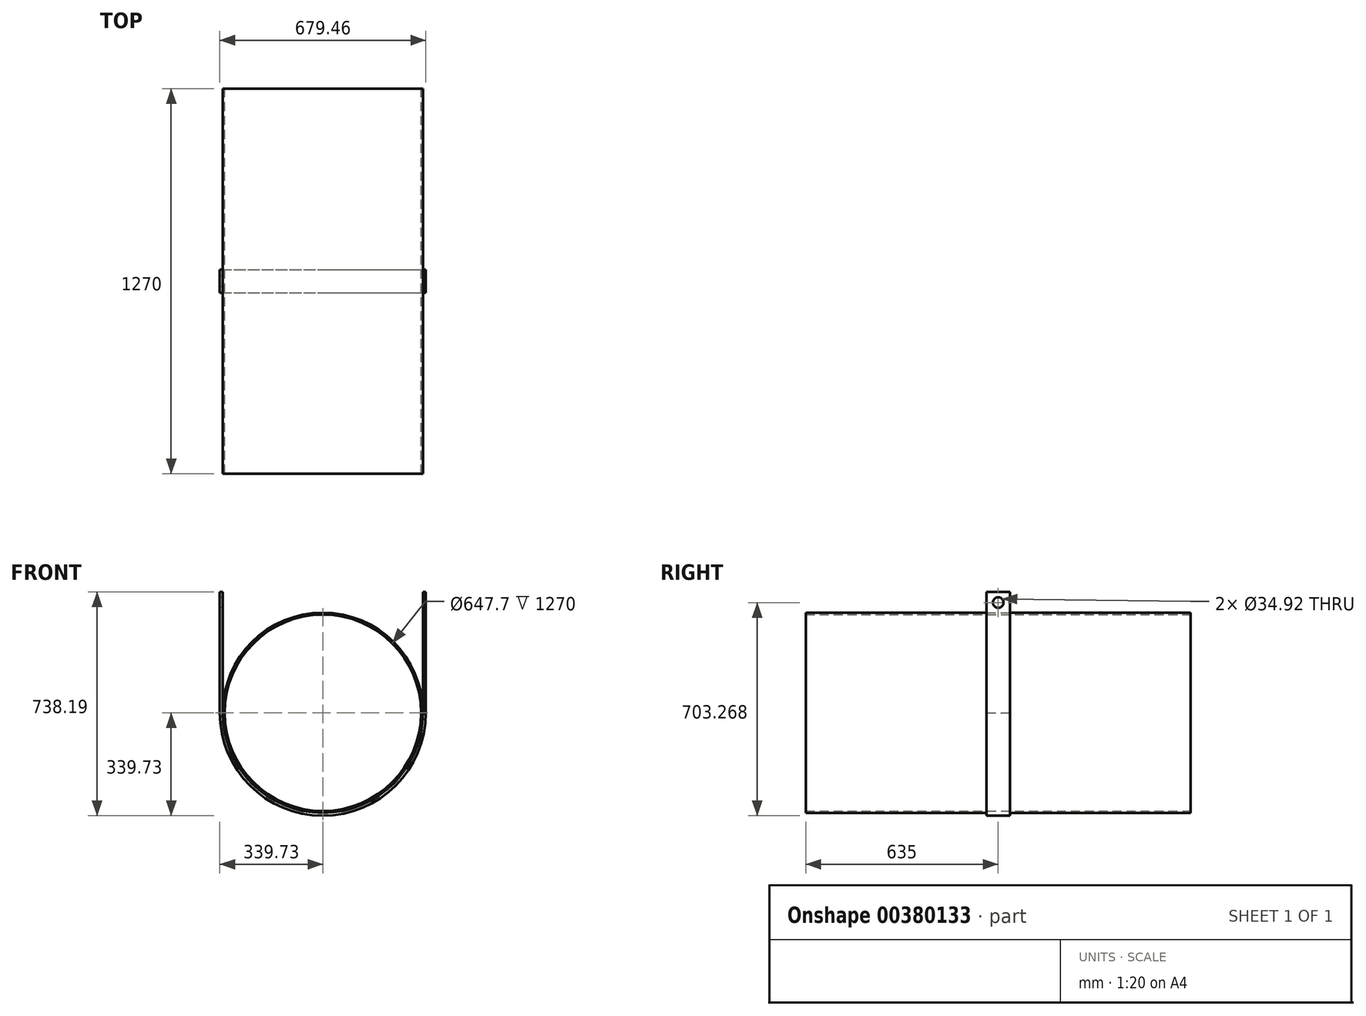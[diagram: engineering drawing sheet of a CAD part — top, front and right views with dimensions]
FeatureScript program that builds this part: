
annotation { "Feature Type Name" : "Feature", "Feature Type Description" : "" }
export const myFeature = defineFeature(function(context is Context, id is Id, definition is map)
    precondition{}
    {
        {
            var Q0;
            Q0=qCreatedBy(makeId("Front.planeOp"),FACE);
            var sketch = newSketch(context, id + "F0", { "sketchPlane" : qUnion([Q0])});
            skArc(sketch, "E0", {"start": v(-330.2, 0) * mm, "mid": v(0, -330.2) * mm, "end": v(330.2, 0) * mm});
            skArc(sketch, "E1", {"start": v(-339.73, 0) * mm, "mid": v(0, -339.73) * mm, "end": v(339.73, 0) * mm});
            skLineSegment(sketch, "E2", {"start": v(-330.2, 0) * mm, "end": v(-330.2, 398.46) * mm});
            skLineSegment(sketch, "E3", {"start": v(-330.2, 398.46) * mm, "end": v(-339.73, 398.46) * mm});
            skLineSegment(sketch, "E4", {"start": v(-339.73, 398.46) * mm, "end": v(-339.73, 0) * mm});
            skLineSegment(sketch, "E5.MirrorCS", {"start": v(330.2, 0) * mm, "end": v(330.2, 398.46) * mm});
            skLineSegment(sketch, "E6.MirrorCS", {"start": v(330.2, 398.46) * mm, "end": v(339.73, 398.46) * mm});
            skLineSegment(sketch, "E7.MirrorCS", {"start": v(339.73, 398.46) * mm, "end": v(339.73, 0) * mm});
            skSolve(sketch);
        }
        {
            var Q0;
            Q0 = qSketchRegion(id + "F0", true);
            extrude(context, id + "F1", {"entities" : qUnion([Q0]), "depth" : 76.2 * mm, "symmetric" : true});
        }
        {
            var Q0;
            Q0=makeQuery(id+"F1.opExtrude","SWEPT_FACE",FACE,{"disambiguationData":[OSD([sQuery(id+"F0.wireOp",EDGE,"E4")])]});
            var sketch = newSketch(context, id + "F2", { "sketchPlane" : qUnion([Q0])});
            skCircle(sketch, "E8", {"center": v(0, 363.54) * mm, "radius": 17.46 * mm});
            skSolve(sketch);
        }
        {
            var Q0;
            Q0 = qSketchRegion(id + "F2", true);
            extrude(context, id + "F3", {"entities" : qUnion([Q0]), "operationType" : NewBodyOperationType.REMOVE, "endBound" : BoundingType.THROUGH_ALL, "oppositeDirection" : true, "depth" : 25.4 * mm});
        }
        {
            var Q0;
            Q0=qCreatedBy(makeId("Front.planeOp"),FACE);
            var sketch = newSketch(context, id + "F4", { "sketchPlane" : qUnion([Q0])});
            skCircle(sketch, "E9", {"center": v(0, 0) * mm, "radius": 330.2 * mm});
            skCircle(sketch, "E10", {"center": v(0, 0) * mm, "radius": 323.85 * mm});
            skSolve(sketch);
        }
        {
            var Q0;
            Q0=makeQuery(id+"F4.imprint","IMPRINT",FACE,{"disambiguationData":[TD([[makeQuery(id+"F4.imprint","IMPRINT",EDGE,{"derivedFrom":sQuery(id+"F4.wireOp",EDGE,"E9")}),1.0]])]});
            extrude(context, id + "F5", {"entities" : qUnion([Q0]), "operationType" : NewBodyOperationType.ADD, "depth" : 1270 * mm, "symmetric" : true});
        }
    });
